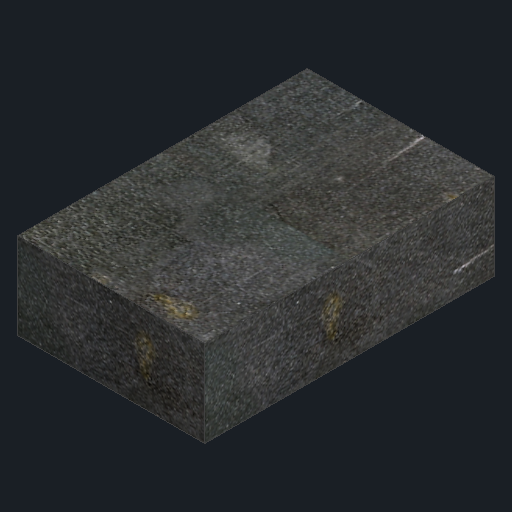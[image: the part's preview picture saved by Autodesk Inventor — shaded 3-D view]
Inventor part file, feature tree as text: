
AUTODESK INVENTOR PART (.ipt)
format: ipt  version: 2022 (Build 260153070, 153G)  size: 307,712 bytes
history: native  units: mm
features: other x1, extrude x1, sketch x1
ambient origin geometry x8: Origin, YZ Plane, XZ Plane, XY Plane, X Axis, Y Axis, Z Axis, Center Point
bodies: Body1 (feature_tree)
feature tree (3):
  other  "Твердое тело1"
  extrude  "Выдавливание1"  Depth=82.0mm
  sketch  "Эскиз1"
